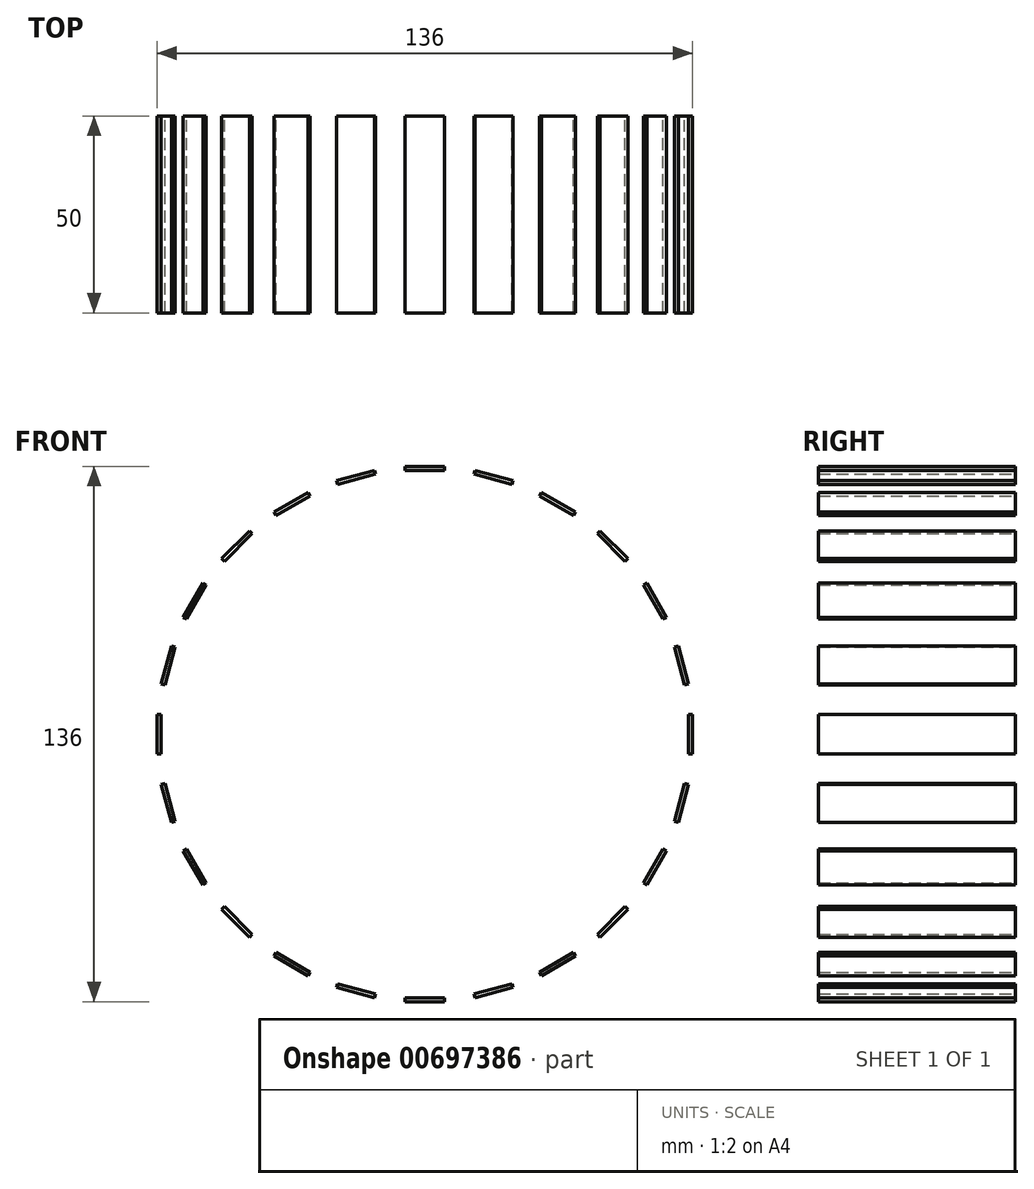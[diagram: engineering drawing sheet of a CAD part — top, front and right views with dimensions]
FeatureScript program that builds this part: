
annotation { "Feature Type Name" : "Feature", "Feature Type Description" : "" }
export const myFeature = defineFeature(function(context is Context, id is Id, definition is map)
    precondition{}
    {
        {
            var Q0;
            Q0=qCreatedBy(makeId("Front.planeOp"),FACE);
            var sketch = newSketch(context, id + "F0", { "sketchPlane" : qUnion([Q0])});
            skCircle(sketch, "E0", {"center": v(0, 0) * mm, "radius": 5 * mm});
            skLineSegment(sketch, "E1", {"start": v(0, 67) * mm, "end": v(-5, 67) * mm});
            skLineSegment(sketch, "E2", {"start": v(-5, 67) * mm, "end": v(-5, 67) * mm});
            skLineSegment(sketch, "E3", {"start": v(-5, 67) * mm, "end": v(-5, 68) * mm});
            skLineSegment(sketch, "E4", {"start": v(-5, 68) * mm, "end": v(5, 68) * mm});
            skLineSegment(sketch, "E5", {"start": v(0, 67) * mm, "end": v(5, 67) * mm});
            skLineSegment(sketch, "E6", {"start": v(5, 68) * mm, "end": v(5, 67) * mm});
            skSolve(sketch);
        }
        {
            var Q0;
            Q0=makeQuery(id+"F0.imprint","IMPRINT",FACE,{"disambiguationData":[TD([[makeQuery(id+"F0.imprint","IMPRINT",EDGE,{"derivedFrom":sQuery(id+"F0.wireOp",EDGE,"E1")}),-1.0]])]});
            var Q1;
            Q1=makeQuery(id+"F0.imprint","IMPRINT",FACE,{"disambiguationData":[TD([[makeQuery(id+"F0.imprint","IMPRINT",EDGE,{"derivedFrom":sQuery(id+"F0.wireOp",EDGE,"E0")}),1.0]])]});
            extrude(context, id + "F1", {"entities" : qUnion([Q0, Q1]), "depth" : 50 * mm, "offsetDistance" : 25 * mm});
        }
        {
            var Q0;
            Q0=makeQuery(id+"F1.opExtrude","SWEPT_BODY",BODY,{"disambiguationData":[OSD([sQuery(id+"F0.wireOp",EDGE,"E1"),sQuery(id+"F0.wireOp",EDGE,"E3"),sQuery(id+"F0.wireOp",EDGE,"E4"),sQuery(id+"F0.wireOp",EDGE,"E5"),sQuery(id+"F0.wireOp",EDGE,"E6")])]});
            var Q1;
            Q1=makeQuery(id+"F1.opExtrude","SWEPT_FACE",FACE,{"disambiguationData":[OSD([sQuery(id+"F0.wireOp",EDGE,"E0")])]});
            circularPattern(context, id + "F2", {"entities" : qUnion([Q0]), "axis" : qUnion([Q1]), "angle" : 360 * degree, "instanceCount" : 24, "equalSpace" : true});
        }
        {
            var Q0;
            Q0=makeQuery(id+"F1.opExtrude","CAP_FACE",FACE,{"disambiguationData":[OSD([sQuery(id+"F0.wireOp",EDGE,"E0")])],"isStart":false});
            extrude(context, id + "F3", {"entities" : qUnion([Q0]), "operationType" : NewBodyOperationType.REMOVE, "oppositeDirection" : true, "depth" : 50 * mm, "offsetDistance" : 25 * mm});
        }
    });
